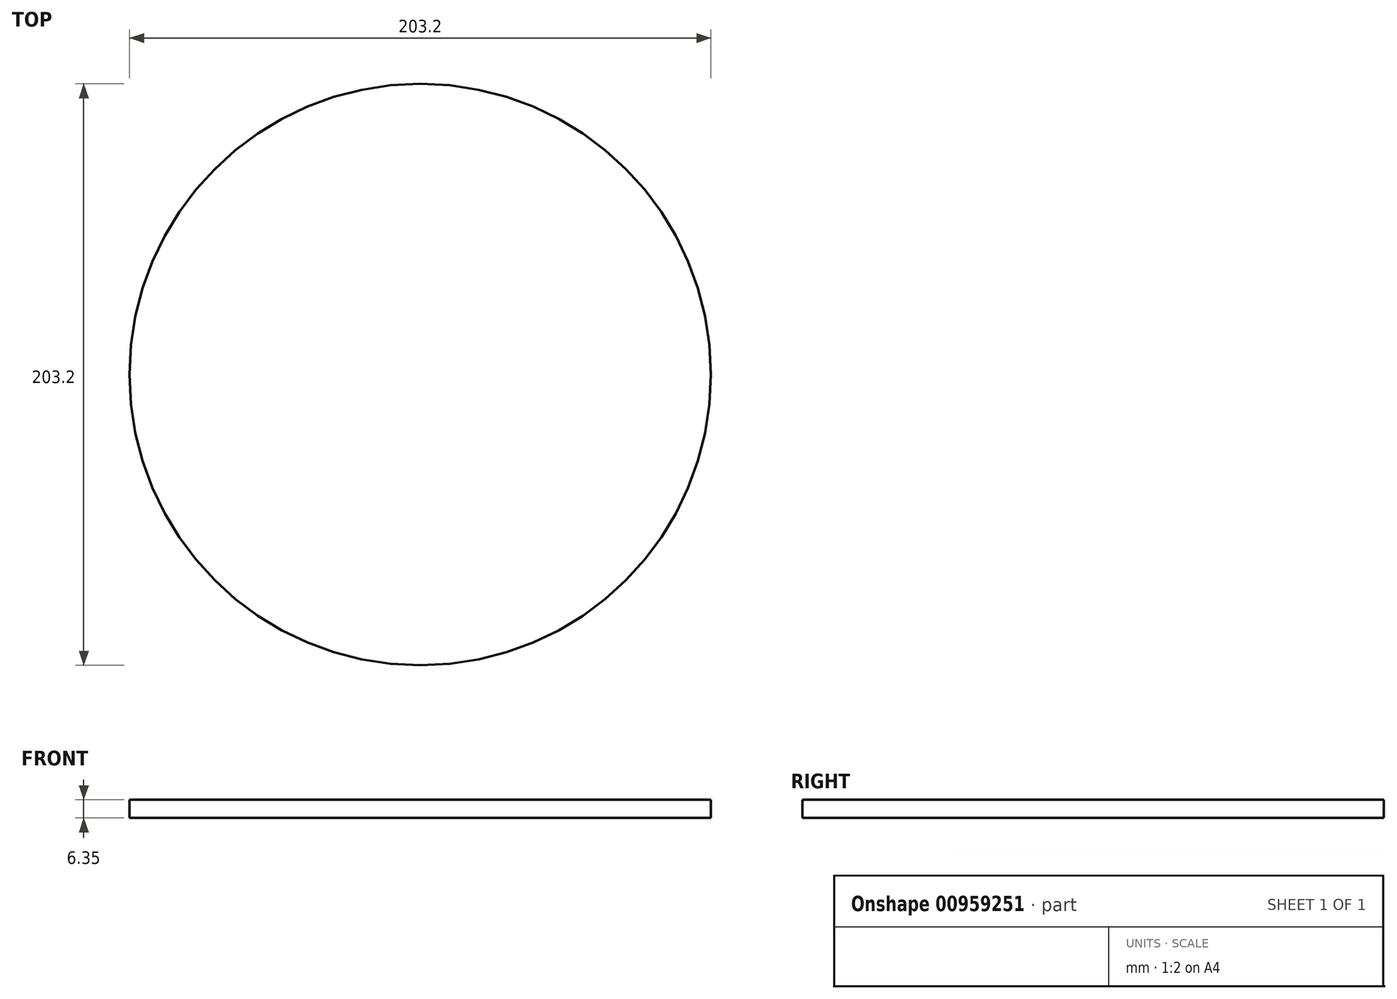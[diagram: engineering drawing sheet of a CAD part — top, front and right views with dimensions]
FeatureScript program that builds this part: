
annotation { "Feature Type Name" : "Feature", "Feature Type Description" : "" }
export const myFeature = defineFeature(function(context is Context, id is Id, definition is map)
    precondition{}
    {
        {
            var Q0;
            Q0=qCreatedBy(makeId("Top.planeOp"),FACE);
            var sketch = newSketch(context, id + "F0", { "sketchPlane" : qUnion([Q0])});
            skCircle(sketch, "E0", {"center": v(0, 0) * mm, "radius": 101.6 * mm});
            skSolve(sketch);
        }
        {
            var Q0;
            Q0 = qSketchRegion(id + "F0", true);
            extrude(context, id + "F1", {"entities" : qUnion([Q0]), "depth" : 6.35 * mm, "offsetDistance" : 25.4 * mm});
        }
    });
